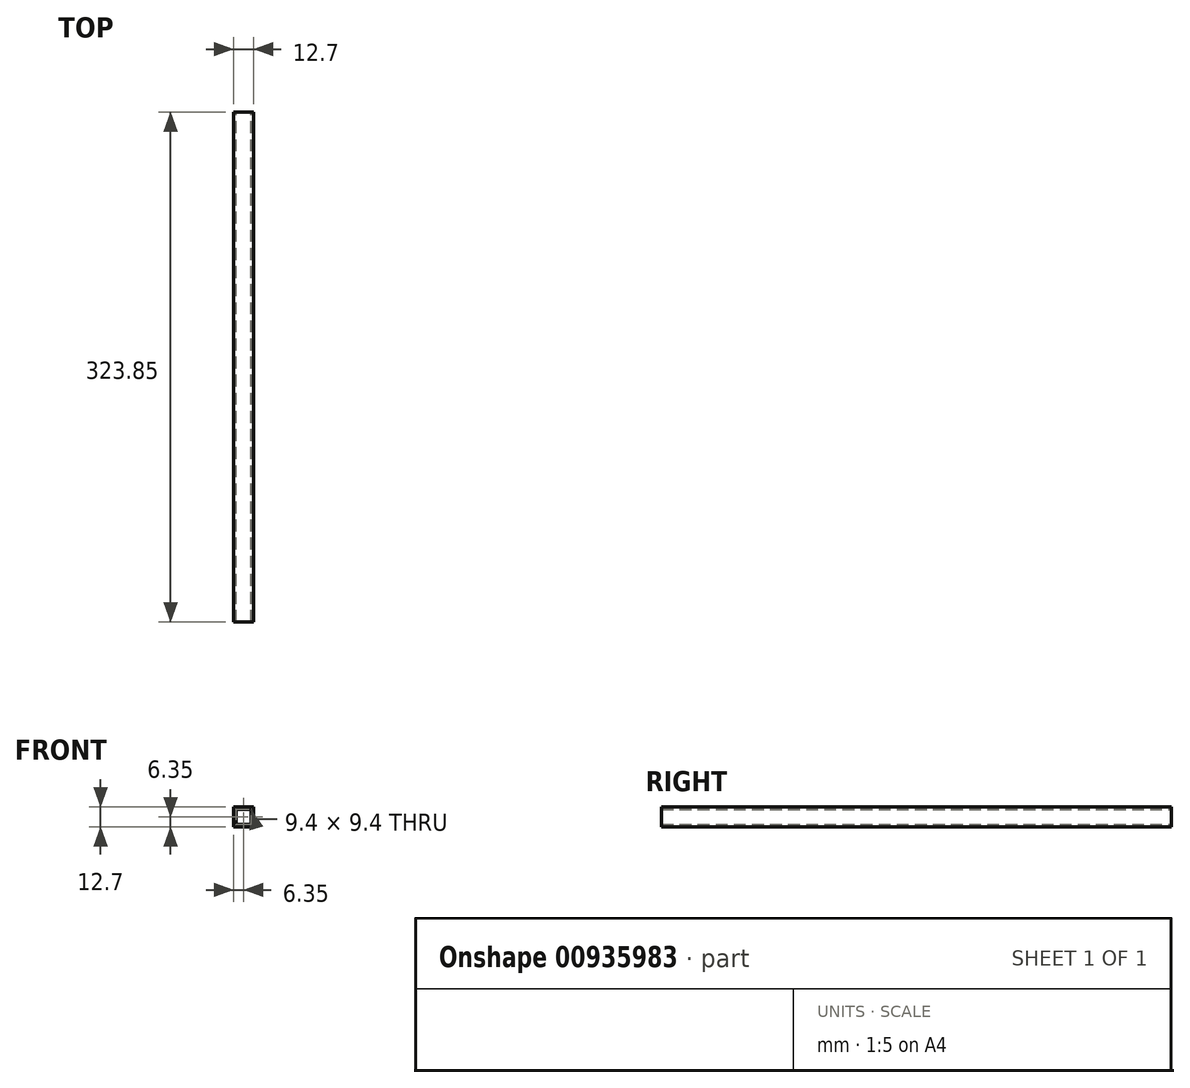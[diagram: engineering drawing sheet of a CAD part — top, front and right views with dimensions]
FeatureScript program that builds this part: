
annotation { "Feature Type Name" : "Feature", "Feature Type Description" : "" }
export const myFeature = defineFeature(function(context is Context, id is Id, definition is map)
    precondition{}
    {
        {
            var Q0;
            Q0=qCreatedBy(makeId("Front.planeOp"),FACE);
            var sketch = newSketch(context, id + "F0", { "sketchPlane" : qUnion([Q0])});
            skLineSegment(sketch, "E0.bottom", {"start": v(6.35, -6.35) * mm, "end": v(-6.35, -6.35) * mm});
            skLineSegment(sketch, "E0.top", {"start": v(6.35, 6.35) * mm, "end": v(-6.35, 6.35) * mm});
            skLineSegment(sketch, "E0.left", {"start": v(6.35, -6.35) * mm, "end": v(6.35, 6.35) * mm});
            skLineSegment(sketch, "E0.right", {"start": v(-6.35, -6.35) * mm, "end": v(-6.35, 6.35) * mm});
            skPoint(sketch, "E0.middle", {"position": v(0, 0) * mm});
            skLineSegment(sketch, "E1.bottom", {"start": v(4.7, -4.7) * mm, "end": v(-4.7, -4.7) * mm});
            skLineSegment(sketch, "E1.top", {"start": v(4.7, 4.7) * mm, "end": v(-4.7, 4.7) * mm});
            skLineSegment(sketch, "E1.left", {"start": v(4.7, -4.7) * mm, "end": v(4.7, 4.7) * mm});
            skLineSegment(sketch, "E1.right", {"start": v(-4.7, -4.7) * mm, "end": v(-4.7, 4.7) * mm});
            skSolve(sketch);
        }
        {
            var Q0;
            Q0=qSketchRegion(id+"F0",true);
            extrude(context, id + "F1", {"entities" : qUnion([Q0]), "depth" : 323.85 * mm, "offsetDistance" : 25.4 * mm});
        }
    });
